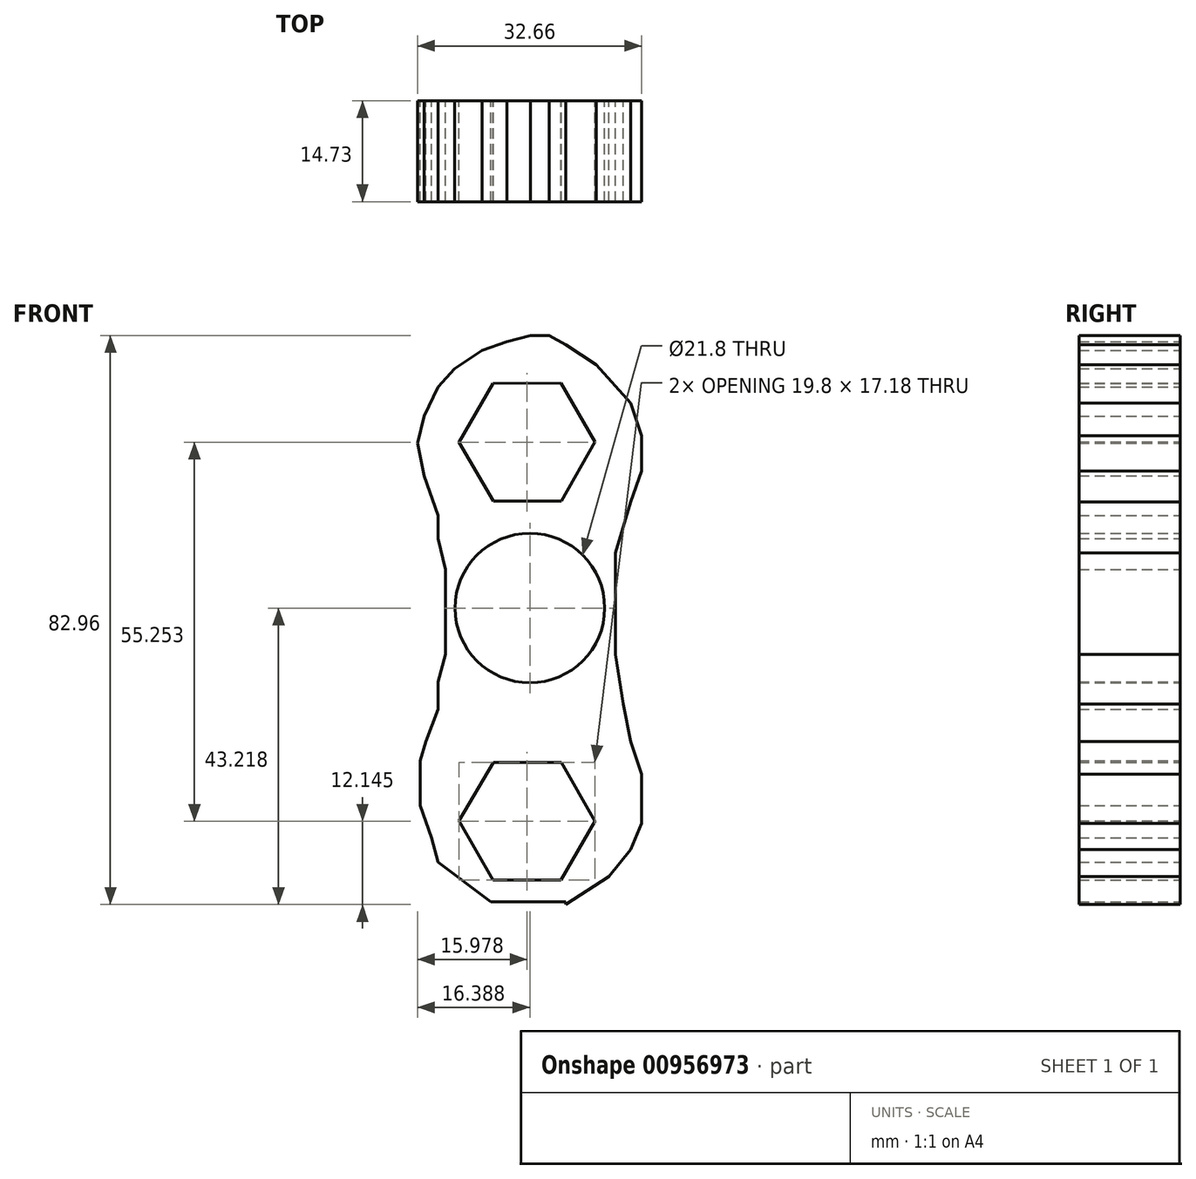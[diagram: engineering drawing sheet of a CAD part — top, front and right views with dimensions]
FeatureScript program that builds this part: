
annotation { "Feature Type Name" : "Feature", "Feature Type Description" : "" }
export const myFeature = defineFeature(function(context is Context, id is Id, definition is map)
    precondition{}
    {
        {
            var Q0;
            Q0=qCreatedBy(makeId("Front.planeOp"),FACE);
            var sketch = newSketch(context, id + "F0", { "sketchPlane" : qUnion([Q0])});
            skLineSegment(sketch, "E0", {"start": v(6.46, 49.5) * mm, "end": v(2.46, 46.76) * mm});
            skLineSegment(sketch, "E1", {"start": v(2.46, 46.76) * mm, "end": v(0, 44.13) * mm});
            skLineSegment(sketch, "E2", {"start": v(0, 44.13) * mm, "end": v(-2.02, 39.84) * mm});
            skLineSegment(sketch, "E3", {"start": v(-2.02, 39.84) * mm, "end": v(-3, 35.94) * mm});
            skLineSegment(sketch, "E4", {"start": v(-3, 35.94) * mm, "end": v(-2.02, 31.17) * mm});
            skLineSegment(sketch, "E5", {"start": v(-2.02, 31.17) * mm, "end": v(0, 25.41) * mm});
            skLineSegment(sketch, "E6", {"start": v(0, 25.41) * mm, "end": v(0, 22) * mm});
            skLineSegment(sketch, "E7", {"start": v(0, 22) * mm, "end": v(1.1, 17.52) * mm});
            skLineSegment(sketch, "E8", {"start": v(1.1, 17.52) * mm, "end": v(1.1, 8.45) * mm});
            skLineSegment(sketch, "E9", {"start": v(1.1, 8.45) * mm, "end": v(1.1, 5.14) * mm});
            skLineSegment(sketch, "E10", {"start": v(1.1, 5.14) * mm, "end": v(0, 1.14) * mm});
            skLineSegment(sketch, "E11", {"start": v(0, 1.14) * mm, "end": v(0, -2.86) * mm});
            skLineSegment(sketch, "E12", {"start": v(0, -2.86) * mm, "end": v(-1.73, -7.54) * mm});
            skLineSegment(sketch, "E13", {"start": v(-1.73, -7.54) * mm, "end": v(-2.61, -10.36) * mm});
            skLineSegment(sketch, "E14", {"start": v(-2.61, -10.36) * mm, "end": v(-2.61, -13.2) * mm});
            skLineSegment(sketch, "E15", {"start": v(-2.61, -13.2) * mm, "end": v(-2.61, -16.9) * mm});
            skLineSegment(sketch, "E16", {"start": v(-2.61, -16.9) * mm, "end": v(-0.95, -21.57) * mm});
            skLineSegment(sketch, "E17", {"start": v(-0.95, -21.57) * mm, "end": v(0, -25.18) * mm});
            skLineSegment(sketch, "E18", {"start": v(0, -25.18) * mm, "end": v(7.72, -30.93) * mm});
            skLineSegment(sketch, "E19", {"start": v(7.72, -30.93) * mm, "end": v(18.64, -30.93) * mm});
            skLineSegment(sketch, "E20", {"start": v(18.64, -31.32) * mm, "end": v(24.88, -27.23) * mm});
            skLineSegment(sketch, "E21", {"start": v(24.88, -27.23) * mm, "end": v(28.1, -23.33) * mm});
            skLineSegment(sketch, "E22", {"start": v(28.1, -23.33) * mm, "end": v(29.66, -19.53) * mm});
            skLineSegment(sketch, "E23", {"start": v(29.66, -19.53) * mm, "end": v(29.66, -16.9) * mm});
            skLineSegment(sketch, "E24", {"start": v(29.66, -16.9) * mm, "end": v(29.66, -12.31) * mm});
            skLineSegment(sketch, "E25", {"start": v(29.66, -12.31) * mm, "end": v(28.1, -7.54) * mm});
            skLineSegment(sketch, "E26", {"start": v(28.1, -7.54) * mm, "end": v(27.03, -2.08) * mm});
            skLineSegment(sketch, "E27", {"start": v(27.03, -2.08) * mm, "end": v(25.86, 5.14) * mm});
            skLineSegment(sketch, "E28", {"start": v(25.86, 5.14) * mm, "end": v(25.86, 12.16) * mm});
            skLineSegment(sketch, "E29", {"start": v(25.86, 12.16) * mm, "end": v(25.86, 19.96) * mm});
            skLineSegment(sketch, "E30", {"start": v(25.86, 19.96) * mm, "end": v(28.1, 27.36) * mm});
            skLineSegment(sketch, "E31", {"start": v(28.1, 27.36) * mm, "end": v(29.66, 31.85) * mm});
            skLineSegment(sketch, "E32", {"start": v(29.66, 31.85) * mm, "end": v(29.66, 37.02) * mm});
            skLineSegment(sketch, "E33", {"start": v(29.66, 37.02) * mm, "end": v(28.1, 41.8) * mm});
            skLineSegment(sketch, "E34", {"start": v(23.03, 47.35) * mm, "end": v(18.64, 50.27) * mm});
            skLineSegment(sketch, "E35", {"start": v(18.64, 50.27) * mm, "end": v(16.2, 51.64) * mm});
            skLineSegment(sketch, "E36", {"start": v(16.2, 51.64) * mm, "end": v(13.48, 51.64) * mm});
            skLineSegment(sketch, "E37", {"start": v(13.48, 51.64) * mm, "end": v(10.07, 50.76) * mm});
            skLineSegment(sketch, "E38", {"start": v(10.07, 50.76) * mm, "end": v(6.46, 49.5) * mm});
            skPoint(sketch, "E39.endSnap0", {"position": v(28.88, 39.4) * mm});
            skPoint(sketch, "E40.endSnap0", {"position": v(20.84, 48.81) * mm});
            skCircle(sketch, "E41", {"center": v(13.39, 11.9) * mm, "radius": 10.9 * mm});
            skLineSegment(sketch, "E42", {"start": v(18.64, -30.93) * mm, "end": v(18.64, -31.32) * mm});
            skLineSegment(sketch, "E43", {"start": v(23.03, 47.35) * mm, "end": v(28.1, 41.8) * mm});
            skCircle(sketch, "E44.cCircle", {"center": v(12.98, 36.08) * mm, "radius": 8.57 * mm, "construction": true});
            skLineSegment(sketch, "E44.0", {"start": v(22.88, 36.1) * mm, "end": v(17.95, 27.52) * mm});
            skLineSegment(sketch, "E44.1", {"start": v(17.95, 27.52) * mm, "end": v(8.05, 27.49) * mm});
            skLineSegment(sketch, "E44.2", {"start": v(8.05, 27.49) * mm, "end": v(3.08, 36.05) * mm});
            skLineSegment(sketch, "E44.3", {"start": v(3.08, 36.05) * mm, "end": v(8, 44.64) * mm});
            skLineSegment(sketch, "E44.4", {"start": v(8, 44.64) * mm, "end": v(17.9, 44.67) * mm});
            skLineSegment(sketch, "E44.5", {"start": v(17.9, 44.67) * mm, "end": v(22.88, 36.1) * mm});
            skPoint(sketch, "E44.0.midPoint", {"position": v(20.42, 31.81) * mm});
            skCircle(sketch, "E45.MirrorC", {"center": v(12.98, -19.17) * mm, "radius": 8.57 * mm, "construction": true});
            skLineSegment(sketch, "E46.MirrorCS", {"start": v(17.9, -27.76) * mm, "end": v(22.88, -19.2) * mm});
            skLineSegment(sketch, "E47.MirrorCS", {"start": v(8, -27.73) * mm, "end": v(17.9, -27.76) * mm});
            skLineSegment(sketch, "E48.MirrorCS", {"start": v(3.08, -19.15) * mm, "end": v(8, -27.73) * mm});
            skLineSegment(sketch, "E49.MirrorCS", {"start": v(8.05, -10.59) * mm, "end": v(3.08, -19.15) * mm});
            skLineSegment(sketch, "E50.MirrorCS", {"start": v(17.95, -10.61) * mm, "end": v(8.05, -10.59) * mm});
            skLineSegment(sketch, "E51.MirrorCS", {"start": v(22.88, -19.2) * mm, "end": v(17.95, -10.61) * mm});
            skSolve(sketch);
        }
        {
            var Q0;
            Q0=makeQuery(id+"F0.imprint","IMPRINT",FACE,{"disambiguationData":[TD([[makeQuery(id+"F0.imprint","IMPRINT",EDGE,{"derivedFrom":sQuery(id+"F0.wireOp",EDGE,"E0")}),1.0]])]});
            extrude(context, id + "F1", {"entities" : qUnion([Q0]), "depth" : 14.73 * mm, "offsetDistance" : 25.4 * mm});
        }
    });
